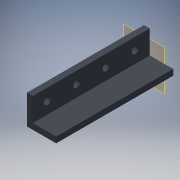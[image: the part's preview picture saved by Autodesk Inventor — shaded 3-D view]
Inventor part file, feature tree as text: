
AUTODESK INVENTOR PART (.ipt)
format: ipt  version: 2016 (Build 200138000, 138)  size: 164,864 bytes
history: native  units: in
note: dims shown in document units (in); Inventor stores cm internally (conversion verified against a paired STEP export)
features: other x21, reference x10, sketch x3, hole x2, fillet x2, plane x1, extrude x1
ambient origin geometry x8: Origin, YZ Plane, XZ Plane, XY Plane, X Axis, Y Axis, Z Axis, Center Point
bodies: Body1 (feature_tree)
feature tree (40):
  other  "A_19"
  other  "A_20"
  other  "A_21"
  other  "A_22"
  other  "A_23"
  other  "A_24"
  other  "A_25"
  other  "A_26"
  other  "A_27"
  other  "A_28"
  other  "A_29"
  other  "A_30"
  other  "A_31"
  other  "A_32"
  other  "A_33"
  other  "A_34"
  other  "A_35"
  other  "A_36"
  other  "FRONT"
  other  "TOP"
  other  "RIGHT"
  plane  "Work Plane4"
  extrude  "Extrusion1"  Depth=0.0787in
  hole  "Hole1"  [1 undecoded]
  hole  "Hole2"  [1 undecoded]
  fillet  "Fillet1"  [1 undecoded]
  fillet  "Fillet2"  [1 undecoded]
  sketch  "Sketch1"  dims[d0=3.1496in d1=0.0in]
  sketch  "Sketch2"  dims[d2=0.1457in d3=0.2362in d4=0.1575in d5=0.0787in d6=90.0deg d7=0.315in d8=0.8108in]
  reference  "Reference1"
  reference  "Reference2"
  reference  "Reference3"
  reference  "Reference4"
  sketch  "Sketch3"  dims[d9=0.1457in d10=0.2362in d11=0.1575in d12=0.0787in d13=90.0deg d14=0.315in d15=0.8108in d16=0.0787in d17=0.0787in]
  reference  "Reference5"
  reference  "Reference6"
  reference  "Reference7"
  reference  "Reference8"
  reference  "Reference9"
  reference  "Reference10"
note: 4 required parameter values undecoded (feature->parameter linkage not recoverable at this tier; creation-order binding heuristic only, values carry confidence <= 0.55)
